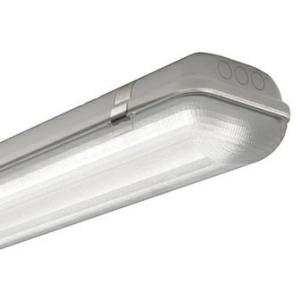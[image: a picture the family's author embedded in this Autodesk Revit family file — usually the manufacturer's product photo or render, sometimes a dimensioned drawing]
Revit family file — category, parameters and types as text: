
# Revit family: 3f_filippi_-_3f_linda_3f_filippi_-_58594_-_3f_linda_led_2x24w_l1270
name_source: partatom
category: Lighting Fixtures
units: mm (PartAtom-declared; Revit-internal decimal feet)

## family parameters
Cut with Voids When Loaded = No
Host = Face
Light Source = No
Part Type = Normal
Room Calculation Point = No
Round Connector Dimension = Use Diameter
Shared = No

## types (1)
- 3F Filippi - 3F Linda (1 x LED, 7911 lm, 54.5 W, 4000 K)
    Apparent Load = 55 VA
    Approval mark = CE
    CIE Flux Codes = 46 76 93 97 100
    Color Rendering = 80
    Color Temperature = 4000 K
    Control Gear = Electronic ballast
    Default Elevation = 1800 mm
    Description = ILLUMINOTECHNICAL
Luminous efficiency 100% (DLOR 97%, ULOR 3%).
Initial luminous flux of the luminaire 7911 lm.
Controlled symmetric distribution.
Installation Interdistance Transv.D = 1.52 x hu - Long.D = 1.17 x hu.
Tabular UGR (CIE 117 - 4H-8H; S=0.25H; 70/50/20): RUG 24.4 - 23.5.
Beam angle: 94° - 78°.
Luminous efficacy 145 lm/W.
Lifetime (L93/B10): 30000 h. (tq+25°C)
Lifetime (L90/B10): 50000 h. (tq+25°C)
Lifetime (L85/B10): 80000 h. (tq+25°C)
Lifetime (L80/B10): 100000 h. (tq+25°C)
Lifetime (L85/B10): 50000 h. (tq+35°C)
Sudden decreased luminous flux after 50000 hours: 0% (C0).
Photobiological safety in compliance with IEC/TR 62778: RG0 risk exempt, (IEC 62471).
In compliance with IEC/EN 62722-2-1 - IEC/EN 62717 standards.

SOURCE
2 linear LED modules 24W/840.
Energy efficiency class (UE 2019/2020 - UE 2019/2015): D.
CIE 13.3 Colour rendering index: CRI >80 (R9 <50%).
IES TM-30 Fidelity Index: Rf = 84 Rg = 95.
CCT nominal colour temperature 4000 K.
Colour initial tolerance (MacAdam): SDCM 3.

MECHANICAL
Self-extinguishing V2 polycarbonate housing, injection moulded, RAL 7035 grey.
Ecologic anti-aging injected sealing gasket.
Diffuser in self-extinguishing V2 polycarbonate, photo-engraved interior, UV stabilised, injection moulded with smooth outer surface, tamper-proof opening.
Gear-holder reflector in hot-dip galvanised steel, painted with white polyester base.
Snug fit safety snap-lock clips for diffuser mounting in stainless steel, screwdriver opening.
Fixing brackets in stainless steel.
Possibility for technicians to access the interior of the luminaire.
Luminaire with limited surface temperature. - D - (EN 60598-2-24)
Dimensions: 1270x160 mm, height 100 mm. Weight 2.699 kg.
IP66 protection degree.
Mechanical strength to impacts IK10 (20 joule).
Glow-wire test resistance 850°C.

ELECTRICAL
Halogen Free electronic wiring 230V-50/60Hz, power factor 0.97, THD <25%, constant output current, SELV, class I, 1 driver.
Power of the luminaire 54.5 W.
ENEC - CE.
SAFE FLICKER: PstLM=<1 and SVM=<0.4 (IEC TR 61547-1 and IEC TR 63158), to ensure a more comfortable and safe light.
Luminaire compliant with EN 60598-2-22 for power supply from a centralised emergency system CPSS (Central Power Supply System), not incorporated in the luminaire - high risk areas excluded. The default power and flux are 100% in AC and 100% in DC.
Ambient temperature from -20°C to +35°C.
Temperature class T6 max 85°C.
Relative humidity UR: <85%.

INSTALLATION
Ceiling / Suspended / Wall.
All accessories dedicated to this product are available on the Catalog and on our website www.3F-Filippi.com.

APPLICATIONS
Suitable product for food production plants (HACCP), IFS (Food Version 6), BRC (GSFS Food Version 7).
Dry, dusty indoor environments, subject to occasional water splashes.
Virtually shatterproof polycarbonate compatibly with the fumes / atmospheres that compromise the elasticity of plastic materials.
Not suitable for installation on surfaces subject to important vibrations, exposed to weather conditions, on ropes or poles.
Suitable for illumination of public car parks and parking grounds referred to DIN 67528:2018-04.

WARNING
Fixture not suitable for cold stores with an ambient temperature <0°C and/or relative humidity >85%.
Luminaire designed for disposal/recycling at end-of-life.
Replaceable (LED only) light source by a professional. Replaceable control gear by a professional.
    Height = 100 mm  [stored 0.328084 ft]
    Lamp = 1 x LED
    Lamp Light Flux = 7911 lm
    Lamp Power = 54.5 W
    Lamp count = 1
    Length = 1270 mm
    Lifetime = 50000 h
    Luminous efficacy = 145 lm/W
    Manufacturer = 3F Filippi
    ModVariant = No
    Model = 3F Filippi - 58594 - 3F Linda LED 2x24W L1270
    Mounting Place = Ceiling
    Mounting Type = Pendant
    Number of Poles = 1
    OnlyDefault = Yes
    Power Factor = 1
    Product Name = 3F Filippi - 3F Linda
    Product group = pendant luminaire
    ProductGroupID = 9
    Protection Class = Protection class I
    Protection Degree = IP 66
    RLX_Detail_Level = 1
    RLX_Emergency_Light_Flux = 0 lm
    RLX_Emergency_Type = 0
    RLX_Emergency_Type_DB = No
    RlxData = <blob elided: 71277 chars, md5=ac3e5305>
    Socket = socket
    Standby Power = 0 W
    System Light Flux = 7911 lm
    System Power = 55 W
    Type Comments = Product without accessories
    Type Image = 3ffilippi_3f_linda_led_2x.jpg
    URL = http://relux.com
    VarID = ---
    Voltage = 0 V
    Weight = 0.00 kg
    Width = 160 mm

note: [stored X ft] marks values corroborated as IEEE doubles in the binary element streams (Revit-internal decimal feet)

## geometry (parser evidence)
native form markers: Blend x4, Sweep x9
no freeform markers — native parametric forms only
